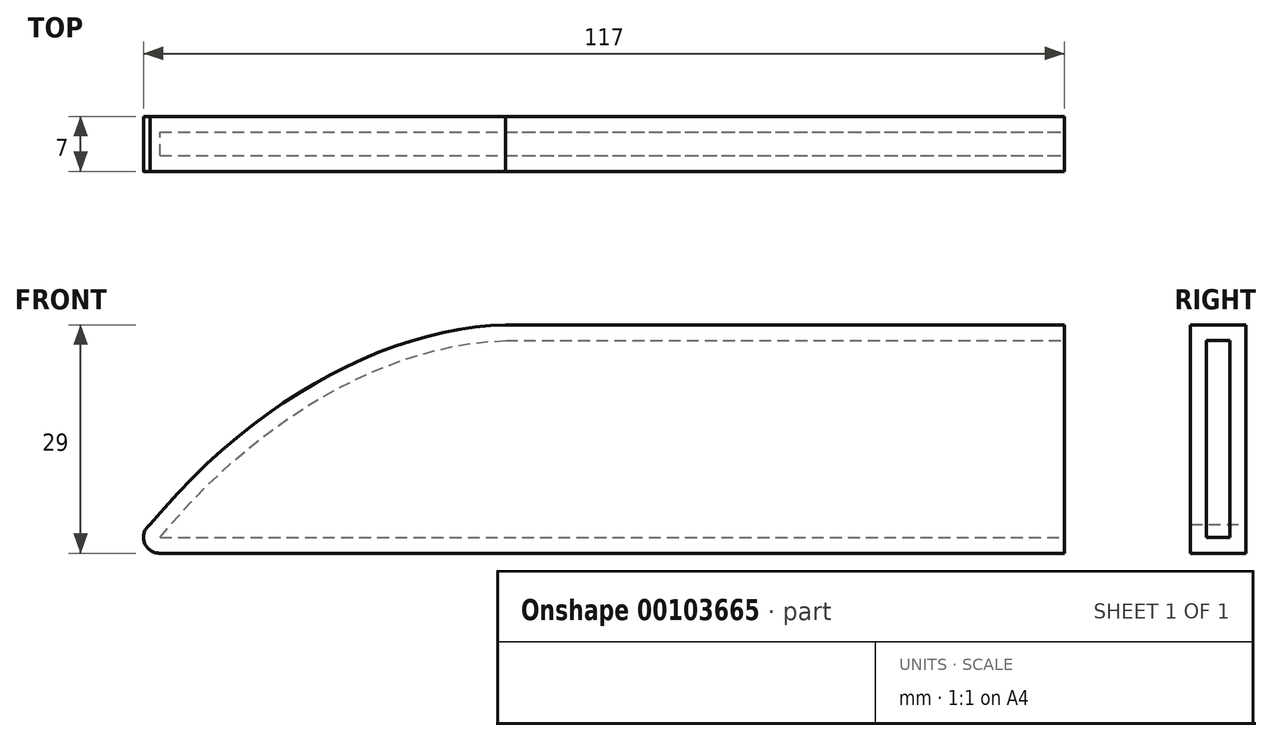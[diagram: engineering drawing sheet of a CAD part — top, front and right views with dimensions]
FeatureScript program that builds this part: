
annotation { "Feature Type Name" : "Feature", "Feature Type Description" : "" }
export const myFeature = defineFeature(function(context is Context, id is Id, definition is map)
    precondition{}
    {
        {
            var Q0;
            Q0=qCreatedBy(makeId("Front.planeOp"),FACE);
            var sketch = newSketch(context, id + "F0", { "sketchPlane" : qUnion([Q0])});
            skLineSegment(sketch, "E0.bottom", {"start": v(-56.93, 3.1) * mm, "end": v(58.07, 3.1) * mm});
            skLineSegment(sketch, "E0.top", {"start": v(-12.93, 32.1) * mm, "end": v(58.07, 32.1) * mm});
            skLineSegment(sketch, "E0.right", {"start": v(58.07, 3.1) * mm, "end": v(58.07, 32.1) * mm});
            skPoint(sketch, "E0.middle", {"position": v(-1.86, 17.6) * mm});
            skArc(sketch, "E1.filletArc", {"start": v(-58.07, 6.75) * mm, "mid": v(-58.84, 4.5) * mm, "end": v(-56.93, 3.1) * mm});
            skFitSpline(sketch, "E2", {"points": [v(-58.07, 6.75) * mm, v(-12.93, 32.1) * mm, v(20.77, 20.03) * mm], "startDerivative": vector(71.86, 87.37) * mm, "endDerivative": vector(71.4, -43.48) * mm});
            skSolve(sketch);
        }
        {
            var Q0;
            Q0=makeQuery(id+"F0.imprint","IMPRINT",FACE,{"disambiguationData":[TD([[makeQuery(id+"F0.imprint","IMPRINT",EDGE,{"derivedFrom":sQuery(id+"F0.wireOp",EDGE,"E0.bottom")}),1.0]])]});
            extrude(context, id + "F1", {"entities" : qUnion([Q0]), "depth" : 7 * mm});
        }
        {
            var Q0;
            Q0=makeQuery(id+"F1.opExtrude","SWEPT_FACE",FACE,{"disambiguationData":[OSD([sQuery(id+"F0.wireOp",EDGE,"WQKhSIT2-V4Xd-IY8b-aeZj-W4uutbFwx66Y.right")])]});
            var Q1;
            Q1=makeQuery(id+"F1.opExtrude","SWEPT_FACE",FACE,{"disambiguationData":[OSD([sQuery(id+"F0.wireOp",EDGE,"E0.right")])]});
            shell(context, id + "F2", {"entities" : qUnion([Q0, Q1]), "thickness" : 2 * mm});
        }
    });
